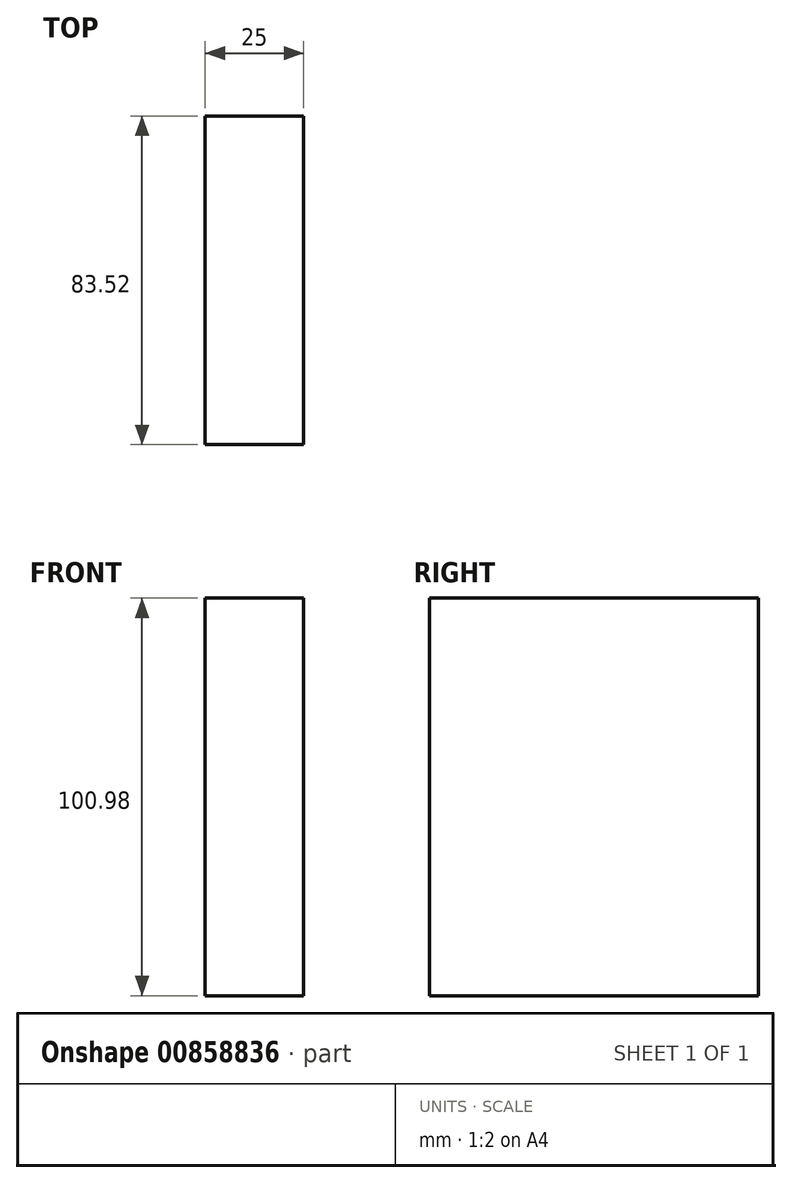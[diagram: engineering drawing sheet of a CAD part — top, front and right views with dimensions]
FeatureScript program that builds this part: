
annotation { "Feature Type Name" : "Feature", "Feature Type Description" : "" }
export const myFeature = defineFeature(function(context is Context, id is Id, definition is map)
    precondition{}
    {
        {
            var Q0;
            Q0=qCreatedBy(makeId("Right.planeOp"),FACE);
            var sketch = newSketch(context, id + "F0", { "sketchPlane" : qUnion([Q0])});
            skLineSegment(sketch, "E0.bottom", {"start": v(0, 45.14) * mm, "end": v(83.52, 45.14) * mm});
            skLineSegment(sketch, "E0.top", {"start": v(0, -55.84) * mm, "end": v(83.52, -55.84) * mm});
            skLineSegment(sketch, "E0.left", {"start": v(0, 45.14) * mm, "end": v(0, -55.84) * mm});
            skLineSegment(sketch, "E0.right", {"start": v(83.52, 45.14) * mm, "end": v(83.52, -55.84) * mm});
            skSolve(sketch);
        }
        {
            var Q0;
            Q0=makeQuery(id+"F0.imprint","IMPRINT",FACE,{"disambiguationData":[TD([[makeQuery(id+"F0.imprint","IMPRINT",EDGE,{"derivedFrom":sQuery(id+"F0.wireOp",EDGE,"E0.bottom")}),-1.0]])]});
            extrude(context, id + "F1", {"entities" : qUnion([Q0]), "depth" : 25 * mm, "offsetDistance" : 25.4 * mm});
        }
    });
